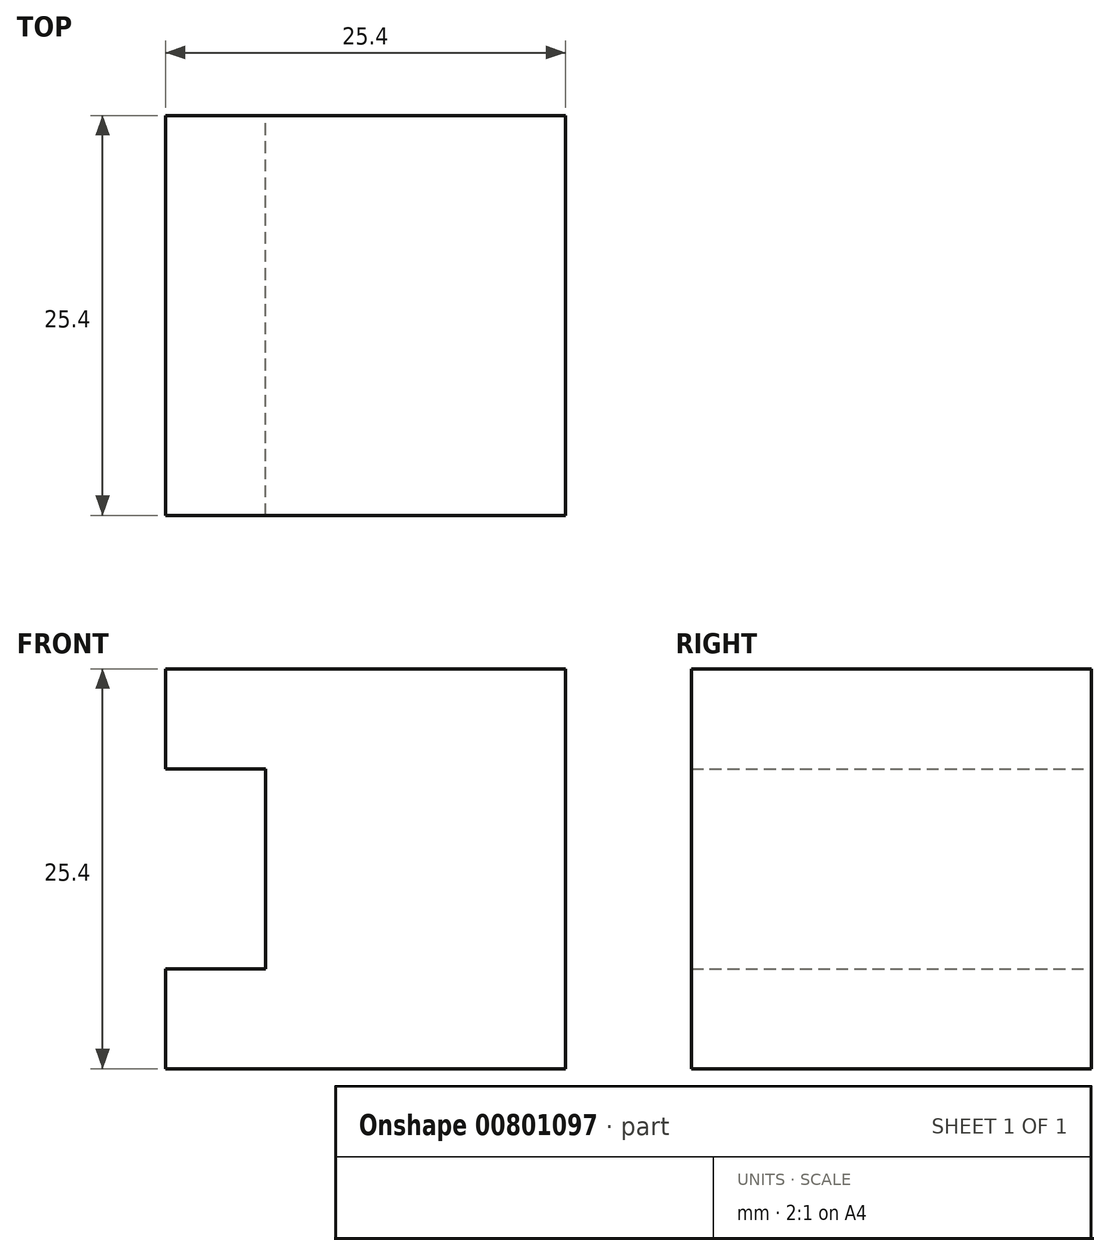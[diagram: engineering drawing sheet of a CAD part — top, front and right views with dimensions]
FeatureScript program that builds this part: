
annotation { "Feature Type Name" : "Feature", "Feature Type Description" : "" }
export const myFeature = defineFeature(function(context is Context, id is Id, definition is map)
    precondition{}
    {
        {
            var Q0;
            Q0=qCreatedBy(makeId("Front.planeOp"),FACE);
            var sketch = newSketch(context, id + "F0", { "sketchPlane" : qUnion([Q0])});
            skLineSegment(sketch, "E0", {"start": v(0, 0) * mm, "end": v(12.7, 0) * mm});
            skLineSegment(sketch, "E1", {"start": v(0, 0) * mm, "end": v(0, 6.35) * mm});
            skLineSegment(sketch, "E2", {"start": v(0, 6.35) * mm, "end": v(6.35, 6.35) * mm});
            skLineSegment(sketch, "E3", {"start": v(6.35, 6.35) * mm, "end": v(6.35, 19.05) * mm});
            skLineSegment(sketch, "E4", {"start": v(6.35, 19.05) * mm, "end": v(0, 19.05) * mm});
            skLineSegment(sketch, "E5", {"start": v(0, 19.05) * mm, "end": v(0, 25.4) * mm});
            skLineSegment(sketch, "E6", {"start": v(0, 25.4) * mm, "end": v(25.4, 25.4) * mm});
            skLineSegment(sketch, "E7", {"start": v(25.4, 25.4) * mm, "end": v(25.4, 0) * mm});
            skLineSegment(sketch, "E8", {"start": v(25.4, 0) * mm, "end": v(0, 0) * mm});
            skSolve(sketch);
        }
        {
            var Q0;
            {var subQ0=sQuery(id+"F0.wireOp",EDGE,"E1");Q0=makeQuery(id+"F0.imprint","IMPRINT",FACE,{"disambiguationData":[TD([[makeQuery(id+"F0.imprint","IMPRINT",EDGE,{"derivedFrom":subQ0}),-1.0]])]});}
            extrude(context, id + "F1", {"entities" : qUnion([Q0]), "depth" : 25.4 * mm, "offsetDistance" : 25.4 * mm});
        }
    });
